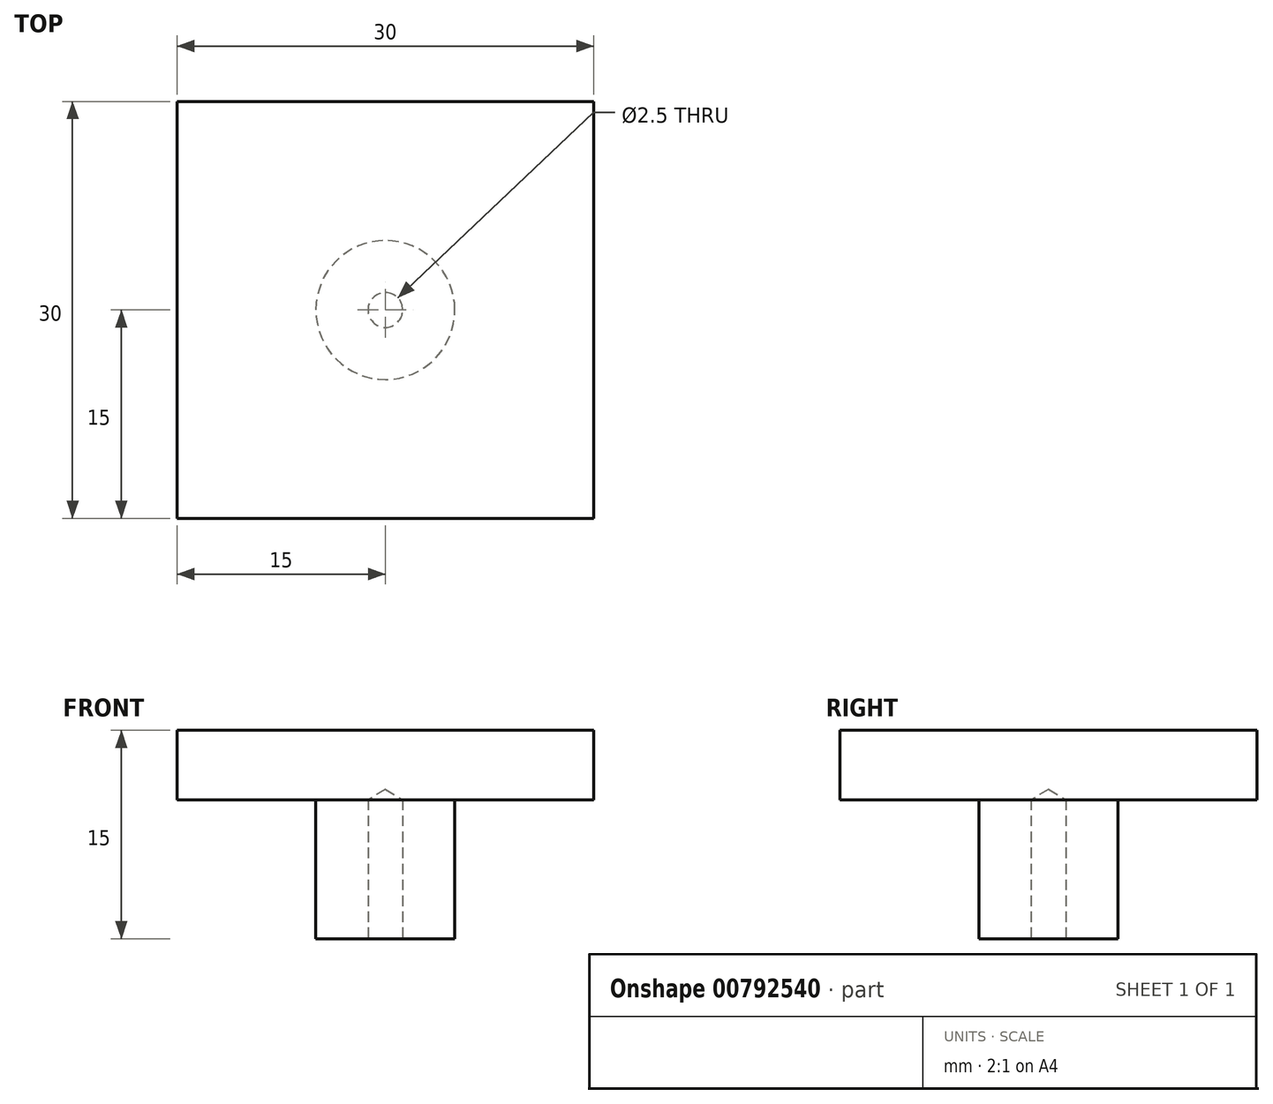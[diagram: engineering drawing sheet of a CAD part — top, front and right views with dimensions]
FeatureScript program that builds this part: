
annotation { "Feature Type Name" : "Feature", "Feature Type Description" : "" }
export const myFeature = defineFeature(function(context is Context, id is Id, definition is map)
    precondition{}
    {
        {
            var Q0;
            Q0=qCreatedBy(makeId("Top.planeOp"),FACE);
            var sketch = newSketch(context, id + "F0", { "sketchPlane" : qUnion([Q0])});
            skCircle(sketch, "E0", {"center": v(0, 0) * mm, "radius": 5 * mm});
            skLineSegment(sketch, "E1.bottom", {"start": v(-15, 15) * mm, "end": v(15, 15) * mm});
            skLineSegment(sketch, "E1.top", {"start": v(-15, -15) * mm, "end": v(15, -15) * mm});
            skLineSegment(sketch, "E1.left", {"start": v(-15, 15) * mm, "end": v(-15, -15) * mm});
            skLineSegment(sketch, "E1.right", {"start": v(15, 15) * mm, "end": v(15, -15) * mm});
            skLineSegment(sketch, "E2", {"start": v(-15, 15) * mm, "end": v(15, -15) * mm, "construction": true});
            skSolve(sketch);
        }
        {
            var Q0;
            Q0=makeQuery(id+"F0.imprint","IMPRINT",FACE,{"disambiguationData":[TD([[makeQuery(id+"F0.imprint","IMPRINT",EDGE,{"derivedFrom":sQuery(id+"F0.wireOp",EDGE,"E0")}),1.0]])]});
            extrude(context, id + "F1", {"entities" : qUnion([Q0]), "oppositeDirection" : true, "depth" : 15 * mm, "offsetDistance" : 25 * mm});
        }
        {
            var Q0;
            Q0=makeQuery(id+"F0.imprint","IMPRINT",FACE,{"disambiguationData":[TD([[makeQuery(id+"F0.imprint","IMPRINT",EDGE,{"derivedFrom":sQuery(id+"F0.wireOp",EDGE,"E0")}),-1.0]])]});
            extrude(context, id + "F2", {"entities" : qUnion([Q0]), "operationType" : NewBodyOperationType.ADD, "oppositeDirection" : true, "depth" : 5 * mm, "offsetDistance" : 25 * mm});
        }
        {
            var Q0;
            Q0=makeQuery(id+"F1.opExtrude","CAP_FACE",FACE,{"disambiguationData":[OSD([sQuery(id+"F0.wireOp",EDGE,"E0")])],"isStart":false});
            var sketch = newSketch(context, id + "F3", { "sketchPlane" : qUnion([Q0])});
            skCircle(sketch, "E3", {"center": v(0, 0) * mm, "radius": 1.25 * mm});
            skSolve(sketch);
        }
        {
            var Q0;
            Q0=sQuery(id+"F3.wireOp",VERTEX,"E3.center");
            var Q1;
            Q1=makeQuery(id+"F1.opExtrude","SWEPT_BODY",BODY,{"disambiguationData":[OSD([sQuery(id+"F0.wireOp",EDGE,"E0")])]});
            hole(context, id + "F4", {"style" : HoleStyle.SIMPLE, "endStyle" : HoleEndStyle.BLIND, "holeDiameter" : 2.5 * mm, "majorDiameter" : 5 * mm, "holeDepth" : 10 * mm, "isTappedThrough" : true, "tappedDepth" : 12 * mm, "tapClearance" : 3, "locations" : qUnion([Q0]), "scope" : qUnion([Q1])});
        }
    });
